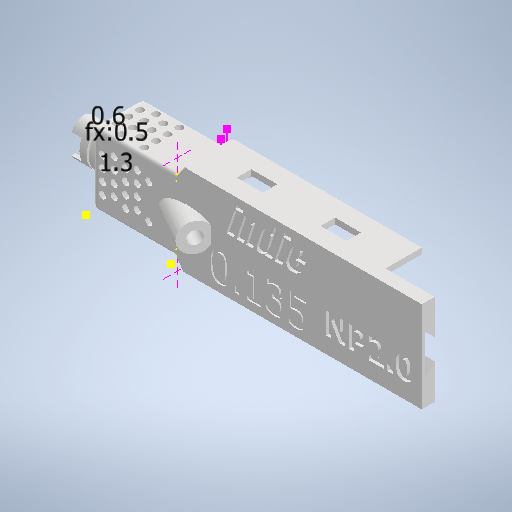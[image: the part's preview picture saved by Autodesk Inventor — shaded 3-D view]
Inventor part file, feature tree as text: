
AUTODESK INVENTOR PART (.ipt)
format: ipt  version: 2025 (Build 290162000, 162)  size: 1,394,688 bytes
history: native  units: in
note: dims shown in document units (in); Inventor stores cm internally (conversion verified against a paired STEP export)
features: extrude x20, reference x13, other x10, sketch x10, fillet x7, projected_geometry x3, plane x2, loft x1, chamfer x1
ambient origin geometry x8: Origin, YZ Plane, XZ Plane, XY Plane, X Axis, Y Axis, Z Axis, Center Point
bodies: Solid1 (feature_tree)
feature tree (67):
  extrude  "dovetail_base"  Depth=0.0031in
  extrude  "tip_offset"  Depth=0.0053in
  extrude  "enclosure_proximal"  Depth=0.1378in
  extrude  "enclosure_front"  TaperAngle=0.0deg  [1 undecoded]
  extrude  "tip_enclosure"  Depth=0.0197in TaperAngle=0.0deg
  extrude  "tip_sealing"  Depth=0.0157in
  extrude  "Extrusion23"  Depth=0.0157in
  other  "screw_planeheight"
  other  "screw_workplane"
  extrude  "screw_support"  Depth=0.0157in TaperAngle=0.0deg
  extrude  "cement_aid_front"  TaperAngle=120.0deg  [1 undecoded]
  extrude  "cement_aid_back"  Depth=0.0315in
  extrude  "cement_aid_left"  Depth=1.0in TaperAngle=0.0deg
  extrude  "cement_aid_right"  Depth=0.0354in
  plane  "Work Plane5"
  extrude  "top_enclosure"  Depth=0.0315in
  loft  "Loft1"
  extrude  "flex_holder"  Depth=0.0236in
  extrude  "top_side_cover"  Depth=0.0512in
  extrude  "screw_hole"  Depth=0.0197in
  fillet  "Fillet4"  Radius=0.0276in
  fillet  "Fillet5"  Radius=0.0472in
  fillet  "Fillet6"  Radius=0.0787in
  chamfer  "Chamfer2"  Distance=0.0551in
  extrude  "cover_holes"  Depth=0.0276in
  fillet  "Fillet7"  Radius=0.0276in
  fillet  "Fillet10"  Radius=0.0197in
  fillet  "Fillet11"  Radius=0.0315in
  fillet  "Fillet12"  Radius=0.0315in
  plane  "Work Plane6"
  extrude  "capilary_block_ring_distal"  Depth=0.0315in
  extrude  "capilary_block_ring_close"  Depth=0.0315in
  extrude  "capilary_block_hole"  Depth=0.0315in
  other  "text"
  other  "tol_text"
  sketch  "Sketch1"  dims[d6=0.0002in d7=0.0031in]
  reference  "Reference1"
  reference  "Reference2"
  reference  "Reference3"
  reference  "Reference4"
  reference  "Reference5"
  reference  "Reference6"
  reference  "Reference7"
  reference  "Reference8"
  reference  "Reference9"
  reference  "Reference10"
  reference  "Reference11"
  reference  "Reference12"
  reference  "Reference13"
  sketch  "Sketch12"  dims[d8=0.0053in d9=0.0053in]
  sketch  "Sketch13"  dims[d10=0.1614in d11=0.1378in]
  sketch  "Sketch15"  dims[d12=0.0354in d13=0.0in]
  other  "Edges1"
  other  "Edges2"
  sketch  "Sketch19"  dims[d14=0.8661in d15=0.0in d16=0.0197in d17=0.0in]
  sketch  "Sketch24"  dims[d18=0.1339in d19=0.0157in]
  other  "text_sketch"
  projected_geometry  "Projected Loop1"
  sketch  "Sketch26"  dims[d20=0.0157in d21=0.0157in]
  projected_geometry  "Projected Loop2"
  sketch  "Sketch27"  dims[d22=0.2165in d23=0.0in d24=0.0157in d25=0.0in]
  projected_geometry  "Projected Loop3"
  sketch  "Sketch29"  dims[d82=0.3268in d83=120.0deg]
  sketch  "Sketch31"  dims[d84=0.0787in d87=0.0315in d88=1.0in d89=0.0in d90=0.0354in d91=0.0315in d92=1.0in d93=0.0in d94=0.0236in d95=0.0512in d96=0.0197in d99=0.0276in d100=0.0472in d101=0.0787in d102=0.0in d103=0.0551in d104=0.0276in d105=0.0276in d106=0.0in d107=0.0197in d108=0.0315in d109=0.0315in d110=0.0315in d111=0.0315in d115=0.0315in d116=0.0315in d117=0.0315in d118=0.0315in d119=0.0315in d126=0.0315in d127=0.0315in d128=0.0315in d129=0.0315in d130=0.0315in d133=0.0315in d135=0.0315in d136=0.0315in d137=0.0315in d138=0.0315in d141=0.0315in d142=0.0315in d144=0.0197in d145=0.0315in d146=0.0315in d147=0.0315in d148=0.0315in d151=0.0236in d152=0.0276in d153=1.0in d154=0.0in d155=0.0118in d156=0.0in d157=0.0315in d159=0.0197in d160=0.0315in d161=0.0315in d162=0.0315in d163=0.0315in d164=0.0197in d165=0.0315in d166=0.0315in d167=0.0315in d168=0.0315in d171=0.0315in d172=0.0315in d173=0.0315in d174=0.0197in d175=0.0315in d176=0.0315in d177=0.0197in d178=0.0315in d179=0.0315in d180=0.0315in d181=0.0315in d182=0.0315in d183=0.0197in d184=0.0118in d185=0.0in d186=1.0in d187=0.0in d188=0.0787in d189=0.0157in d190=0.0157in d191=0.0157in d194=0.0591in d195=0.0in d196=0.0in d197=90.0deg d198=0.0in d199=90.0deg d200=0.0236in d201=0.2106in d202=0.0984in d203=0.0079in d205=0.0394in d206=0.0in d207=0.354in d208=0.0in d209=0.0079in d210=0.0079in d211=0.0197in d215=0.0079in d216=0.0197in d217=45.0deg d231=0.0394in d232=0.0709in d233=0.1575in d235=0.0472in d236=0.3937in d237=0.0in d238=0.0315in d240=0.0787in d243=0.0197in d245=0.0236in d246=0.0236in d247=0.0236in d248=0.0315in d249=0.0315in d250=0.0315in d251=0.0315in d252=0.1181in d253=0.1181in d254=0.0118in d255=0.0118in d256=0.0079in d257=0.0in d258=0.1339in d260=0.0118in d261=0.1929in d262=0.0965in d263=0.1929in d264=0.0965in d265=0.0197in d266=0.0236in d267=0.0039in d268=0.0in d269=0.0157in d270=0.0394in d271=0.0in d273=0.0059in d274=0.0787in d275=0.0394in d278=0.0197in d279=0.0in d280=0.0433in d281=0.0236in d282=-0.0394in d283=0.0236in d284=0.0354in d285=0.0118in d286=0.0in d287=0.0197in d288=0.0in d290=0.0in d291=0.0in d292=0.0472in d293=0.0591in d241=0.0344in d242=0.0197in]
  parser-record x1  (decoder bookkeeping rows leaked as tree rows — omitted from the tree; the rows remain in map.json)
  other  "np2_full_assembly.iam"
  other  "Neuropixels_20_metal cap_NPM_FLEX_01-01-009:1"
note: 2 required parameter values undecoded (feature->parameter linkage not recoverable at this tier; creation-order binding heuristic only, values carry confidence <= 0.55)
note: 1 file-system path scrubbed to <path> (originals preserved in map.json)
